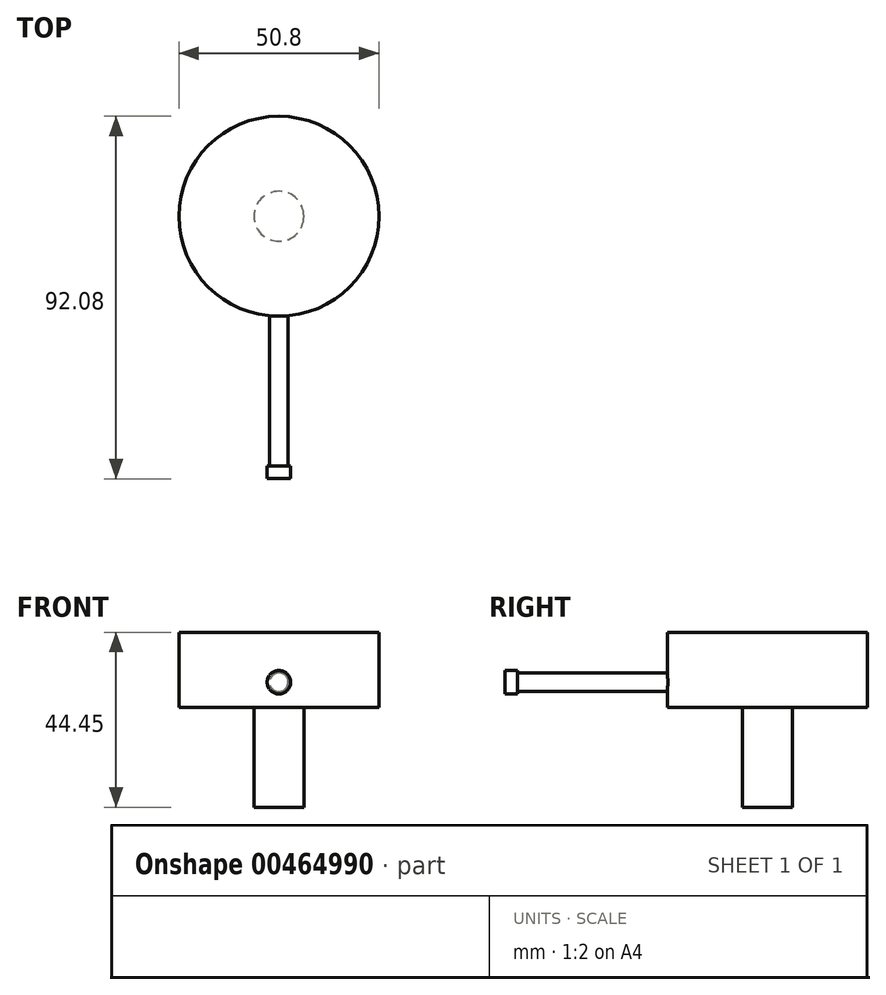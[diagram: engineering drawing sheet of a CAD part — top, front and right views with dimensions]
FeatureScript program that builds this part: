
annotation { "Feature Type Name" : "Feature", "Feature Type Description" : "" }
export const myFeature = defineFeature(function(context is Context, id is Id, definition is map)
    precondition{}
    {
        {
            var Q0;
            Q0=qCreatedBy(makeId("Top.planeOp"),FACE);
            var sketch = newSketch(context, id + "F0", { "sketchPlane" : qUnion([Q0])});
            skCircle(sketch, "E0", {"center": v(0, 0) * mm, "radius": 25.4 * mm});
            skSolve(sketch);
        }
        {
            var Q0;
            Q0=makeQuery(id+"F0.imprint","IMPRINT",FACE,{"disambiguationData":[TD([[makeQuery(id+"F0.imprint","IMPRINT",EDGE,{"derivedFrom":sQuery(id+"F0.wireOp",EDGE,"E0")}),1.0]])]});
            extrude(context, id + "F1", {"entities" : qUnion([Q0]), "depth" : 19.05 * mm});
        }
        {
            var Q0;
            Q0=makeQuery(id+"F1.opExtrude","CAP_FACE",FACE,{"disambiguationData":[OSD([sQuery(id+"F0.wireOp",EDGE,"E0")])],"isStart":false});
            var sketch = newSketch(context, id + "F2", { "sketchPlane" : qUnion([Q0])});
            skCircle(sketch, "E1.0", {"center": v(0, 0) * mm, "radius": 22.23 * mm});
            skSolve(sketch);
        }
        {
            var Q0;
            Q0=makeQuery(id+"F2.imprint","IMPRINT",FACE,{"disambiguationData":[TD([[makeQuery(id+"F2.imprint","IMPRINT",EDGE,{"derivedFrom":sQuery(id+"F2.wireOp",EDGE,"E1.0")}),-1.0]])]});
            extrude(context, id + "F3", {"entities" : qUnion([Q0]), "operationType" : NewBodyOperationType.ADD, "oppositeDirection" : true, "depth" : 3.17 * mm});
        }
        {
            var Q0;
            Q0=qCreatedBy(makeId("Front.planeOp"),FACE);
            var sketch = newSketch(context, id + "F4", { "sketchPlane" : qUnion([Q0])});
            skCircle(sketch, "E2", {"center": v(0, 6.35) * mm, "radius": 2.38 * mm});
            skSolve(sketch);
        }
        {
            var Q0;
            Q0 = qSketchRegion(id + "F4", true);
            extrude(context, id + "F5", {"entities" : qUnion([Q0]), "operationType" : NewBodyOperationType.ADD, "depth" : 63.5 * mm});
        }
        {
            var Q0;
            Q0=makeQuery(id+"F5.opExtrude","CAP_FACE",FACE,{"disambiguationData":[OSD([sQuery(id+"F4.wireOp",EDGE,"E2")])],"isStart":false});
            var sketch = newSketch(context, id + "F6", { "sketchPlane" : qUnion([Q0])});
            skCircle(sketch, "E3.0", {"center": v(0, 6.35) * mm, "radius": 8.73 * mm});
            skCircle(sketch, "E4.0", {"center": v(0, 6.35) * mm, "radius": 2.98 * mm});
            skSolve(sketch);
        }
        {
            var Q0;
            Q0=makeQuery(id+"F6.imprint","IMPRINT",FACE,{"disambiguationData":[TD([[makeQuery(id+"F6.imprint","IMPRINT",EDGE,{"derivedFrom":makeQuery(id+"F5.opExtrude","CAP_EDGE",EDGE,{"disambiguationData":[OSD([sQuery(id+"F4.wireOp",EDGE,"E2")])],"isStart":false})}),1.0]])]});
            var Q1;
            Q1=makeQuery(id+"F6.imprint","IMPRINT",FACE,{"disambiguationData":[TD([[makeQuery(id+"F6.imprint","IMPRINT",EDGE,{"derivedFrom":sQuery(id+"F6.wireOp",EDGE,"E4.0")}),1.0]])]});
            extrude(context, id + "F7", {"entities" : qUnion([Q0, Q1]), "operationType" : NewBodyOperationType.ADD, "depth" : 3.17 * mm});
        }
        {
            var Q0;
            Q0=makeQuery(id+"F1.opExtrude","CAP_FACE",FACE,{"disambiguationData":[OSD([sQuery(id+"F0.wireOp",EDGE,"E0")])],"isStart":false});
            var sketch = newSketch(context, id + "F8", { "sketchPlane" : qUnion([Q0])});
            skCircle(sketch, "E5.0", {"center": v(0, 0) * mm, "radius": 22.6 * mm});
            skSolve(sketch);
        }
        {
            var Q0;
            Q0=makeQuery(id+"F8.imprint","IMPRINT",FACE,{"disambiguationData":[TD([[makeQuery(id+"F8.imprint","IMPRINT",EDGE,{"derivedFrom":sQuery(id+"F8.wireOp",EDGE,"E5.0")}),1.0]])]});
            extrude(context, id + "F9", {"entities" : qUnion([Q0]), "operationType" : NewBodyOperationType.ADD, "depth" : -3.17 * mm});
        }
        {
            var Q0;
            Q0=makeQuery(id+"F1.opExtrude","CAP_FACE",FACE,{"disambiguationData":[OSD([sQuery(id+"F0.wireOp",EDGE,"E0")])],"isStart":true});
            var sketch = newSketch(context, id + "F10", { "sketchPlane" : qUnion([Q0])});
            skCircle(sketch, "E6", {"center": v(0, 0) * mm, "radius": 6.35 * mm});
            skSolve(sketch);
        }
        {
            var Q0;
            Q0=makeQuery(id+"F10.imprint","IMPRINT",FACE,{"disambiguationData":[TD([[makeQuery(id+"F10.imprint","IMPRINT",EDGE,{"derivedFrom":sQuery(id+"F10.wireOp",EDGE,"E6")}),1.0]])]});
            extrude(context, id + "F11", {"entities" : qUnion([Q0]), "operationType" : NewBodyOperationType.ADD, "depth" : 25.4 * mm});
        }
    });
